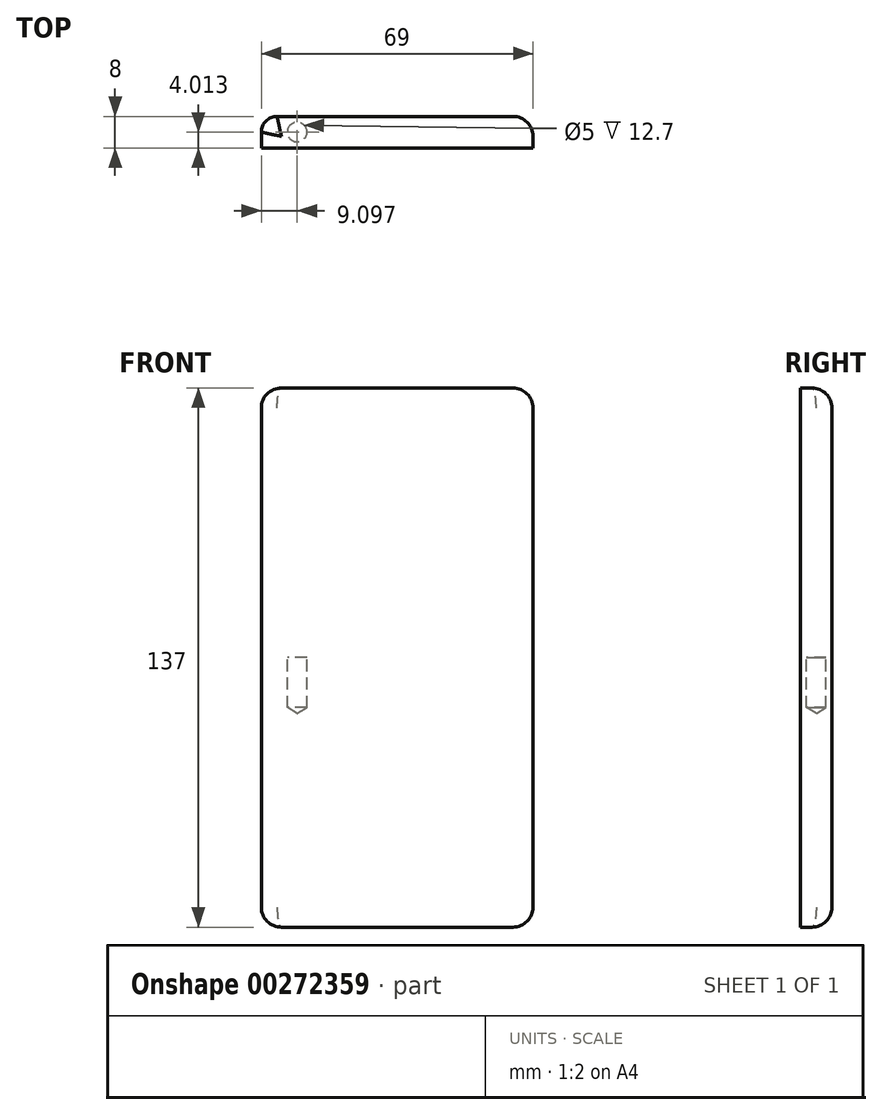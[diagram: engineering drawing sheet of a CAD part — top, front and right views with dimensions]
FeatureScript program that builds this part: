
annotation { "Feature Type Name" : "Feature", "Feature Type Description" : "" }
export const myFeature = defineFeature(function(context is Context, id is Id, definition is map)
    precondition{}
    {
        {
            var Q0;
            Q0=qCreatedBy(makeId("Front.planeOp"),FACE);
            var sketch = newSketch(context, id + "F0", { "sketchPlane" : qUnion([Q0])});
            skLineSegment(sketch, "E0.bottom", {"start": v(34.5, -68.5) * mm, "end": v(-34.5, -68.5) * mm});
            skLineSegment(sketch, "E0.top", {"start": v(34.5, 68.5) * mm, "end": v(-34.5, 68.5) * mm});
            skLineSegment(sketch, "E0.left", {"start": v(34.5, -68.5) * mm, "end": v(34.5, 68.5) * mm});
            skLineSegment(sketch, "E0.right", {"start": v(-34.5, -68.5) * mm, "end": v(-34.5, 68.5) * mm});
            skPoint(sketch, "E0.middle", {"position": v(0, 0) * mm});
            skSolve(sketch);
        }
        {
            var Q0;
            Q0 = qSketchRegion(id + "F0", true);
            extrude(context, id + "F1", {"entities" : qUnion([Q0]), "depth" : 8 * mm});
        }
        {
            var Q0;
            Q0=makeQuery(id+"F1.opExtrude","CAP_EDGE",EDGE,{"disambiguationData":[OSD([sQuery(id+"F0.wireOp",EDGE,"E0.right")])],"isStart":true});
            fillet(context, id + "F2", {"entities" : qUnion([Q0]), "radius" : 4 * mm, "tangentPropagation" : true, "allowEdgeOverflow" : false});
        }
        {
            var Q0;
            Q0=makeQuery(id+"F1.opExtrude","SWEPT_EDGE",EDGE,{"disambiguationData":[OSD([sQuery(id+"F0.wireOp",EDGE,"E0.bottom"),sQuery(id+"F0.wireOp",EDGE,"E0.left")])]});
            fillet(context, id + "F3", {"entities" : qUnion([Q0]), "radius" : 5.08 * mm, "tangentPropagation" : true, "allowEdgeOverflow" : false});
        }
        {
            var Q0;
            {var subQ0=sQuery(id+"F0.wireOp",EDGE,"E0.left");var subQ1=sQuery(id+"F0.wireOp",EDGE,"E0.bottom");Q0=makeQuery(id+"F3.opFillet","BLEND_EDGE",EDGE,{"blendedFrom":[makeQuery(id+"F1.opExtrude","SWEPT_EDGE",EDGE,{"disambiguationData":[OSD([subQ1,subQ0])]}),makeQuery(id+"F1.opExtrude","CAP_FACE",FACE,{"disambiguationData":[OSD([subQ1,sQuery(id+"F0.wireOp",EDGE,"E0.top"),subQ0,sQuery(id+"F0.wireOp",EDGE,"E0.right")])],"isStart":true})],"blendedInto":[makeQuery(id+"F1.opExtrude","CAP_FACE",FACE,{"disambiguationData":[OSD([subQ1,sQuery(id+"F0.wireOp",EDGE,"E0.top"),subQ0,sQuery(id+"F0.wireOp",EDGE,"E0.right")])],"isStart":true})]});}
            fillet(context, id + "F4", {"entities" : qUnion([Q0]), "radius" : 5.08 * mm, "tangentPropagation" : true, "allowEdgeOverflow" : false});
        }
        {
            var Q0;
            Q0=makeQuery(id+"F1.opExtrude","CAP_EDGE",EDGE,{"disambiguationData":[OSD([sQuery(id+"F0.wireOp",EDGE,"E0.top")])],"isStart":true});
            fillet(context, id + "F5", {"entities" : qUnion([Q0]), "radius" : 5.08 * mm, "tangentPropagation" : true, "allowEdgeOverflow" : false});
        }
        {
            var Q0;
            Q0=qCreatedBy(makeId("Top.planeOp"),FACE);
            var sketch = newSketch(context, id + "F6", { "sketchPlane" : qUnion([Q0])});
            skPoint(sketch, "E1", {"position": v(-25.4, -3.99) * mm});
            skSolve(sketch);
        }
        {
            var Q0;
            Q0=sQuery(id+"F6.wireOp",VERTEX,"E1");
            var Q1;
            Q1=makeQuery(id+"F1.opExtrude","SWEPT_BODY",BODY,{"disambiguationData":[OSD([sQuery(id+"F0.wireOp",EDGE,"E0.bottom"),sQuery(id+"F0.wireOp",EDGE,"E0.top"),sQuery(id+"F0.wireOp",EDGE,"E0.left"),sQuery(id+"F0.wireOp",EDGE,"E0.right")])]});
            hole(context, id + "F7", {"style" : HoleStyle.SIMPLE, "endStyle" : HoleEndStyle.BLIND, "holeDiameter" : 5 * mm, "holeDepth" : 12.7 * mm, "tappedDepth" : 12.7 * mm, "tapClearance" : 3, "locations" : qUnion([Q0]), "scope" : qUnion([Q1])});
        }
    });
